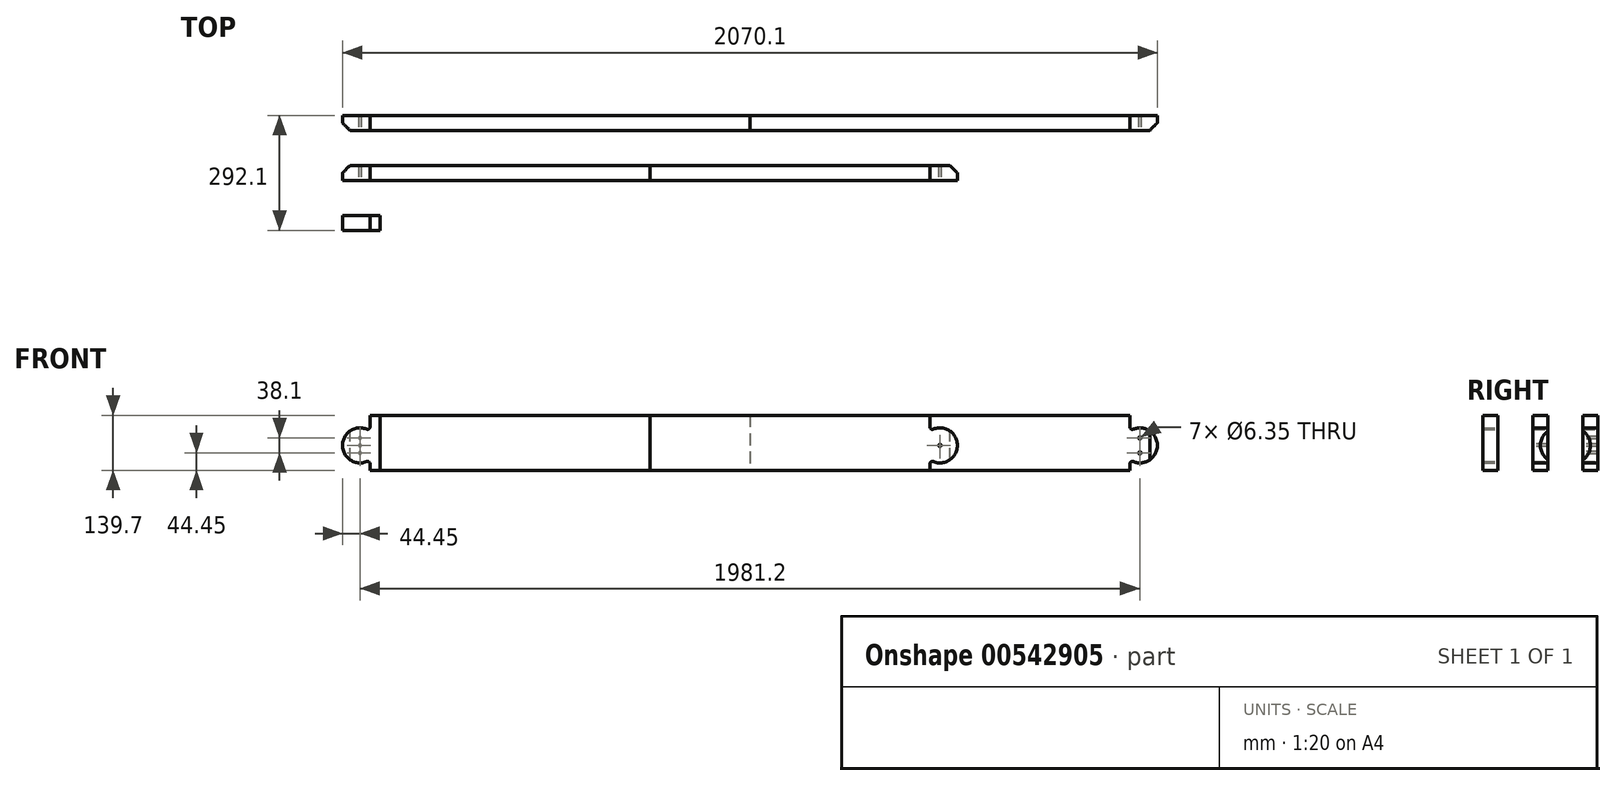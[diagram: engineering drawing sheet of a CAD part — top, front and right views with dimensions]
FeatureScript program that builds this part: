
annotation { "Feature Type Name" : "Feature", "Feature Type Description" : "" }
export const myFeature = defineFeature(function(context is Context, id is Id, definition is map)
    precondition{}
    {
        {
            var Q0;
            Q0=qCreatedBy(makeId("Front.planeOp"),FACE);
            var sketch = newSketch(context, id + "F0", { "sketchPlane" : qUnion([Q0])});
            skArc(sketch, "E0", {"start": v(25.4, 36.48) * mm, "mid": v(-44.45, 0) * mm, "end": v(25.4, -36.48) * mm});
            skLineSegment(sketch, "E1.bottom", {"start": v(50.8, 76.2) * mm, "end": v(25.4, 76.2) * mm});
            skLineSegment(sketch, "E1.top", {"start": v(50.8, -63.5) * mm, "end": v(25.4, -63.5) * mm});
            skLineSegment(sketch, "E1.left", {"start": v(50.8, 76.2) * mm, "end": v(50.8, -63.5) * mm});
            skLineSegment(sketch, "E1.right", {"start": v(25.4, 76.2) * mm, "end": v(25.4, 36.48) * mm});
            skPoint(sketch, "E1.middle", {"position": v(38.1, 6.35) * mm});
            skLineSegment(sketch, "E2.trimOffspring", {"start": v(25.4, -36.48) * mm, "end": v(25.4, -63.5) * mm});
            skSolve(sketch);
        }
        {
            var Q0;
            Q0=makeQuery(id+"F0.imprint","IMPRINT",FACE,{"disambiguationData":[TD([[makeQuery(id+"F0.imprint","IMPRINT",EDGE,{"derivedFrom":sQuery(id+"F0.wireOp",EDGE,"E0")}),1.0]])]});
            extrude(context, id + "F1", {"entities" : qUnion([Q0]), "depth" : 38.1 * mm});
        }
        {
            var Q0;
            Q0=makeQuery(id+"F1.opExtrude","SWEPT_EDGE",EDGE,{"disambiguationData":[OSD([sQuery(id+"F0.wireOp",EDGE,"E0"),sQuery(id+"F0.wireOp",EDGE,"E1.right")])]});
            var Q1;
            Q1=makeQuery(id+"F1.opExtrude","SWEPT_EDGE",EDGE,{"disambiguationData":[OSD([sQuery(id+"F0.wireOp",EDGE,"E0"),sQuery(id+"F0.wireOp",EDGE,"E2.trimOffspring")])]});
            fillet(context, id + "F2", {"entities" : qUnion([Q0, Q1]), "radius" : 6.35 * mm, "tangentPropagation" : true, "allowEdgeOverflow" : false});
        }
        {
            var Q0;
            Q0=makeQuery(id+"F1.opExtrude","SWEPT_BODY",BODY,{"disambiguationData":[OSD([sQuery(id+"F0.wireOp",EDGE,"E0"),sQuery(id+"F0.wireOp",EDGE,"E1.bottom"),sQuery(id+"F0.wireOp",EDGE,"E1.top"),sQuery(id+"F0.wireOp",EDGE,"E1.left"),sQuery(id+"F0.wireOp",EDGE,"E1.right"),sQuery(id+"F0.wireOp",EDGE,"E2.trimOffspring")])]});
            transform(context, id + "F3", {"entities" : qUnion([Q0]), "transformType" : TransformType.TRANSLATION_3D, "dx" : 0 * mm, "dy" : 254 * mm, "dz" : 0 * mm, "makeCopy" : true});
        }
        {
            var Q0;
            Q0=makeQuery(id+"F3.opPattern","COPY",FACE,{"derivedFrom":makeQuery(id+"F1.opExtrude","SWEPT_FACE",FACE,{"disambiguationData":[OSD([sQuery(id+"F0.wireOp",EDGE,"E1.left")])]}),"instanceName":"1"});
            extrude(context, id + "F4", {"entities" : qUnion([Q0]), "operationType" : NewBodyOperationType.ADD, "depth" : 939.8 * mm});
        }
        {
            var Q0;
            {var subQ0=sQuery(id+"F0.wireOp",EDGE,"E1.left");var subQ1=makeQuery(id+"F4.boolean.opBoolean","MERGE",FACE,{"derivedFrom":[makeQuery(id+"F3.opPattern","COPY",FACE,{"derivedFrom":makeQuery(id+"F1.opExtrude","CAP_FACE",FACE,{"disambiguationData":[OSD([sQuery(id+"F0.wireOp",EDGE,"E0"),sQuery(id+"F0.wireOp",EDGE,"E1.bottom"),sQuery(id+"F0.wireOp",EDGE,"E1.top"),subQ0,sQuery(id+"F0.wireOp",EDGE,"E1.right"),sQuery(id+"F0.wireOp",EDGE,"E2.trimOffspring")])],"isStart":false}),"instanceName":"1"}),makeQuery(id+"F4.opExtrude","SWEPT_FACE",FACE,{"disambiguationData":[OSD([subQ0]),TDD([makeQuery(id+"F3.opPattern","COPY",EDGE,{"derivedFrom":makeQuery(id+"F1.opExtrude","CAP_EDGE",EDGE,{"disambiguationData":[OSD([subQ0])],"isStart":false}),"instanceName":"1"})])]})]});Q0=makeQuery(id+"F9.boolean.opBoolean","MERGE",FACE,{"derivedFrom":[subQ1,makeQuery(id+"F9.opPattern","COPY",FACE,{"derivedFrom":subQ1,"instanceName":"1"})]});}
            var sketch = newSketch(context, id + "F5", { "sketchPlane" : qUnion([Q0])});
            skCircle(sketch, "E3", {"center": v(0, 19.05) * mm, "radius": 3.18 * mm});
            skLineSegment(sketch, "E4", {"start": v(0, 0) * mm, "end": v(0, 13.8) * mm, "construction": true});
            skLineSegment(sketch, "E5", {"start": v(0, 0) * mm, "end": v(19.07, 0) * mm, "construction": true});
            skCircle(sketch, "E6.MirrorC", {"center": v(0, -19.05) * mm, "radius": 3.18 * mm});
            skSolve(sketch);
        }
        {
            var Q0;
            Q0=qSketchRegion(id+"F5",true);
            extrude(context, id + "F6", {"entities" : qUnion([Q0]), "operationType" : NewBodyOperationType.REMOVE, "endBound" : BoundingType.THROUGH_ALL, "oppositeDirection" : true, "depth" : 25.4 * mm});
        }
        {
            var Q0;
            Q0=qCreatedBy(makeId("Top.planeOp"),FACE);
            var sketch = newSketch(context, id + "F7", { "sketchPlane" : qUnion([Q0])});
            skLineSegment(sketch, "E7", {"start": v(-63.5, 254) * mm, "end": v(-63.5, 209.79) * mm});
            skLineSegment(sketch, "E8", {"start": v(-63.5, 209.79) * mm, "end": v(-19.29, 209.79) * mm});
            skLineSegment(sketch, "E9", {"start": v(-19.29, 209.79) * mm, "end": v(-63.5, 254) * mm});
            skSolve(sketch);
        }
        {
            var Q0;
            Q0=qSketchRegion(id+"F7",true);
            extrude(context, id + "F8", {"entities" : qUnion([Q0]), "operationType" : NewBodyOperationType.REMOVE, "endBound" : BoundingType.SYMMETRIC, "oppositeDirection" : true, "depth" : 127 * mm});
        }
        {
            var Q0;
            Q0=makeQuery(id+"F3.opPattern","COPY",BODY,{"derivedFrom":makeQuery(id+"F1.opExtrude","SWEPT_BODY",BODY,{"disambiguationData":[OSD([sQuery(id+"F0.wireOp",EDGE,"E0"),sQuery(id+"F0.wireOp",EDGE,"E1.bottom"),sQuery(id+"F0.wireOp",EDGE,"E1.top"),sQuery(id+"F0.wireOp",EDGE,"E1.left"),sQuery(id+"F0.wireOp",EDGE,"E1.right"),sQuery(id+"F0.wireOp",EDGE,"E2.trimOffspring")])]}),"instanceName":"1"});
            var Q1;
            Q1=makeQuery(id+"F4.opExtrude","CAP_FACE",FACE,{"disambiguationData":[OSD([sQuery(id+"F0.wireOp",EDGE,"E1.left")])],"isStart":false});
            mirror(context, id + "F9", {"operationType" : NewBodyOperationType.ADD, "entities" : qUnion([Q0]), "mirrorPlane" : qUnion([Q1])});
        }
        {
            var Q0;
            Q0=makeQuery(id+"F1.opExtrude","SWEPT_BODY",BODY,{"disambiguationData":[OSD([sQuery(id+"F0.wireOp",EDGE,"E0"),sQuery(id+"F0.wireOp",EDGE,"E1.bottom"),sQuery(id+"F0.wireOp",EDGE,"E1.top"),sQuery(id+"F0.wireOp",EDGE,"E1.left"),sQuery(id+"F0.wireOp",EDGE,"E1.right"),sQuery(id+"F0.wireOp",EDGE,"E2.trimOffspring")])]});
            transform(context, id + "F10", {"entities" : qUnion([Q0]), "transformType" : TransformType.TRANSLATION_3D, "dx" : 0 * mm, "dy" : 127 * mm, "dz" : 0 * mm, "makeCopy" : true});
        }
        {
            var Q0;
            Q0=makeQuery(id+"F10.opPattern","COPY",FACE,{"derivedFrom":makeQuery(id+"F1.opExtrude","SWEPT_FACE",FACE,{"disambiguationData":[OSD([sQuery(id+"F0.wireOp",EDGE,"E1.left")])]}),"instanceName":"1"});
            extrude(context, id + "F11", {"entities" : qUnion([Q0]), "operationType" : NewBodyOperationType.ADD, "depth" : 685.8 * mm});
        }
        {
            var Q0;
            {var subQ0=sQuery(id+"F0.wireOp",EDGE,"E1.left");var subQ1=makeQuery(id+"F11.boolean.opBoolean","MERGE",FACE,{"derivedFrom":[makeQuery(id+"F10.opPattern","COPY",FACE,{"derivedFrom":makeQuery(id+"F1.opExtrude","CAP_FACE",FACE,{"disambiguationData":[OSD([sQuery(id+"F0.wireOp",EDGE,"E0"),sQuery(id+"F0.wireOp",EDGE,"E1.bottom"),sQuery(id+"F0.wireOp",EDGE,"E1.top"),subQ0,sQuery(id+"F0.wireOp",EDGE,"E1.right"),sQuery(id+"F0.wireOp",EDGE,"E2.trimOffspring")])],"isStart":false}),"instanceName":"1"}),makeQuery(id+"F11.opExtrude","SWEPT_FACE",FACE,{"disambiguationData":[OSD([subQ0]),TDD([makeQuery(id+"F10.opPattern","COPY",EDGE,{"derivedFrom":makeQuery(id+"F1.opExtrude","CAP_EDGE",EDGE,{"disambiguationData":[OSD([subQ0])],"isStart":false}),"instanceName":"1"})])]})]});Q0=makeQuery(id+"F16.boolean.opBoolean","MERGE",FACE,{"derivedFrom":[subQ1,makeQuery(id+"F16.opPattern","COPY",FACE,{"derivedFrom":subQ1,"instanceName":"1"})]});}
            var sketch = newSketch(context, id + "F12", { "sketchPlane" : qUnion([Q0])});
            skCircle(sketch, "E10", {"center": v(0, 0) * mm, "radius": 3.18 * mm});
            skSolve(sketch);
        }
        {
            var Q0;
            Q0=qSketchRegion(id+"F12",true);
            extrude(context, id + "F13", {"entities" : qUnion([Q0]), "operationType" : NewBodyOperationType.REMOVE, "endBound" : BoundingType.THROUGH_ALL, "oppositeDirection" : true, "depth" : 25.4 * mm});
        }
        {
            var Q0;
            Q0=qCreatedBy(makeId("Top.planeOp"),FACE);
            var sketch = newSketch(context, id + "F14", { "sketchPlane" : qUnion([Q0])});
            skLineSegment(sketch, "E11", {"start": v(-63.5, 88.9) * mm, "end": v(-63.5, 152.4) * mm});
            skLineSegment(sketch, "E12", {"start": v(-63.5, 152.4) * mm, "end": v(0, 152.4) * mm});
            skLineSegment(sketch, "E13", {"start": v(0, 152.4) * mm, "end": v(-63.5, 88.9) * mm});
            skSolve(sketch);
        }
        {
            var Q0;
            Q0=qSketchRegion(id+"F14",true);
            extrude(context, id + "F15", {"entities" : qUnion([Q0]), "operationType" : NewBodyOperationType.REMOVE, "endBound" : BoundingType.SYMMETRIC, "depth" : 101.6 * mm});
        }
        {
            var Q0;
            Q0=makeQuery(id+"F10.opPattern","COPY",BODY,{"derivedFrom":makeQuery(id+"F1.opExtrude","SWEPT_BODY",BODY,{"disambiguationData":[OSD([sQuery(id+"F0.wireOp",EDGE,"E0"),sQuery(id+"F0.wireOp",EDGE,"E1.bottom"),sQuery(id+"F0.wireOp",EDGE,"E1.top"),sQuery(id+"F0.wireOp",EDGE,"E1.left"),sQuery(id+"F0.wireOp",EDGE,"E1.right"),sQuery(id+"F0.wireOp",EDGE,"E2.trimOffspring")])]}),"instanceName":"1"});
            var Q1;
            Q1=makeQuery(id+"F11.opExtrude","CAP_FACE",FACE,{"disambiguationData":[OSD([sQuery(id+"F0.wireOp",EDGE,"E1.left")])],"isStart":false});
            mirror(context, id + "F16", {"operationType" : NewBodyOperationType.ADD, "entities" : qUnion([Q0]), "mirrorPlane" : qUnion([Q1])});
        }
    });
